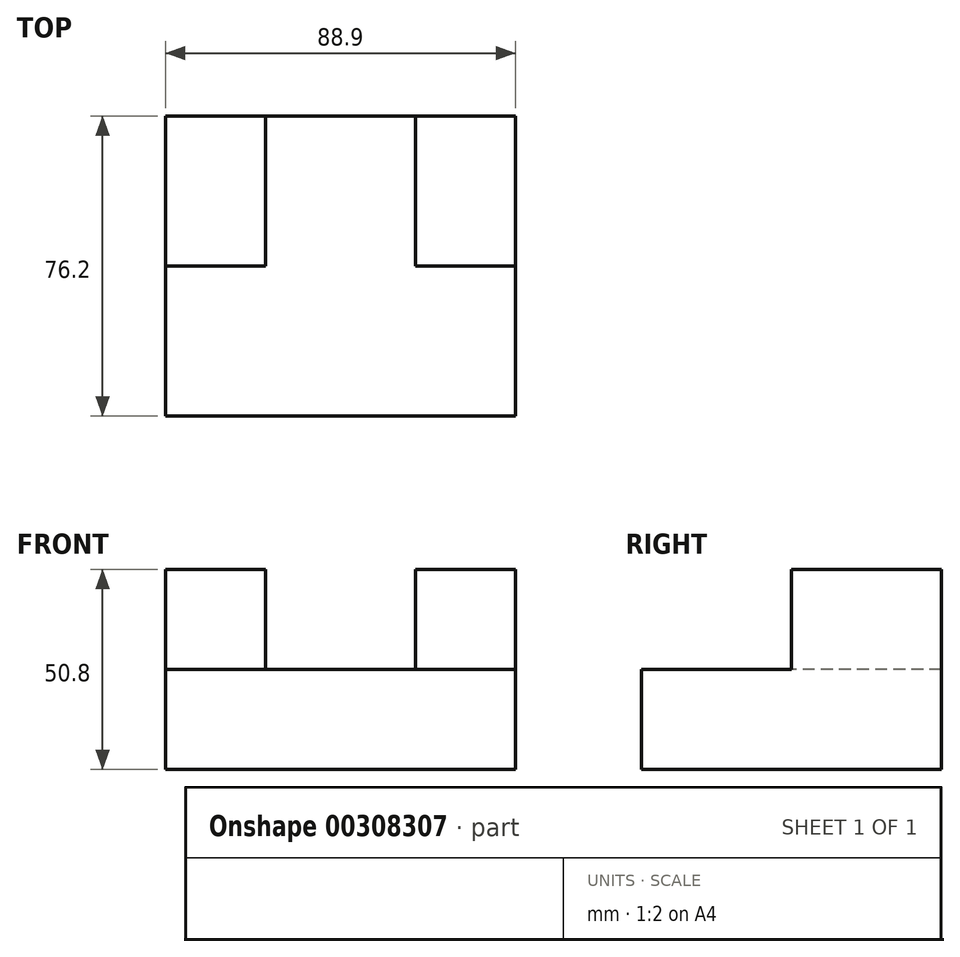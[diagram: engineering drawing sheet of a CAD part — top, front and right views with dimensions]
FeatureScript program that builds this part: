
annotation { "Feature Type Name" : "Feature", "Feature Type Description" : "" }
export const myFeature = defineFeature(function(context is Context, id is Id, definition is map)
    precondition{}
    {
        {
            var Q0;
            Q0=qCreatedBy(makeId("Right.planeOp"),FACE);
            var sketch = newSketch(context, id + "F0", { "sketchPlane" : qUnion([Q0])});
            skLineSegment(sketch, "E0", {"start": v(-37.4, -26.95) * mm, "end": v(38.8, -26.95) * mm});
            skLineSegment(sketch, "E1", {"start": v(-37.4, -26.95) * mm, "end": v(-37.4, -1.55) * mm});
            skLineSegment(sketch, "E2", {"start": v(-37.4, -1.55) * mm, "end": v(0.7, -1.55) * mm});
            skLineSegment(sketch, "E3", {"start": v(0.7, -1.55) * mm, "end": v(0.7, 23.85) * mm});
            skLineSegment(sketch, "E4", {"start": v(0.7, 23.85) * mm, "end": v(38.8, 23.85) * mm});
            skLineSegment(sketch, "E5", {"start": v(38.8, 23.85) * mm, "end": v(38.8, -26.95) * mm});
            skSolve(sketch);
        }
        {
            var Q0;
            Q0=makeQuery(id+"F0.imprint","IMPRINT",FACE,{"disambiguationData":[TD([[makeQuery(id+"F0.imprint","IMPRINT",EDGE,{"derivedFrom":sQuery(id+"F0.wireOp",EDGE,"E0")}),1.0]])]});
            extrude(context, id + "F1", {"entities" : qUnion([Q0]), "oppositeDirection" : true, "depth" : 88.9 * mm});
        }
        {
            var Q0;
            Q0=makeQuery(id+"F1.opExtrude","SWEPT_FACE",FACE,{"disambiguationData":[OSD([sQuery(id+"F0.wireOp",EDGE,"E3")])]});
            var sketch = newSketch(context, id + "F2", { "sketchPlane" : qUnion([Q0])});
            skLineSegment(sketch, "E6.bottom", {"start": v(-63.5, 23.85) * mm, "end": v(-25.4, 23.85) * mm});
            skLineSegment(sketch, "E6.top", {"start": v(-63.5, -1.55) * mm, "end": v(-25.4, -1.55) * mm});
            skLineSegment(sketch, "E6.left", {"start": v(-63.5, 23.85) * mm, "end": v(-63.5, -1.55) * mm});
            skLineSegment(sketch, "E6.right", {"start": v(-25.4, 23.85) * mm, "end": v(-25.4, -1.55) * mm});
            skSolve(sketch);
        }
        {
            var Q0;
            Q0=makeQuery(id+"F2.imprint","IMPRINT",FACE,{"disambiguationData":[TD([[makeQuery(id+"F2.imprint","IMPRINT",EDGE,{"derivedFrom":sQuery(id+"F2.wireOp",EDGE,"E6.bottom")}),-1.0]])]});
            extrude(context, id + "F3", {"entities" : qUnion([Q0]), "operationType" : NewBodyOperationType.REMOVE, "endBound" : BoundingType.THROUGH_ALL, "oppositeDirection" : true, "depth" : 25.4 * mm});
        }
    });
